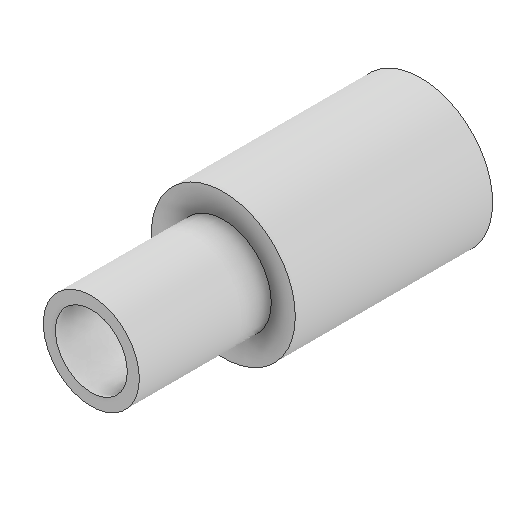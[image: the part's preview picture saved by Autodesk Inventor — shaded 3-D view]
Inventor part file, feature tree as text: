
AUTODESK INVENTOR PART (.ipt)
format: ipt  version: 2025.1 (Build 291241000, 241)  size: 116,736 bytes
history: native  units: mm
features: extrude x2, other x1, sketch x1
ambient origin geometry x8: Origin, YZ Plane, XZ Plane, XY Plane, X Axis, Y Axis, Z Axis, Center Point
bodies: Body1 (feature_tree)
feature tree (4):
  other  "Bryła1"
  sketch  "Szkic1"
  extrude  "Wyciągnięcie proste1"  Depth=3.0mm
  extrude  "Wyciągnięcie proste2"  Depth=4.0mm
